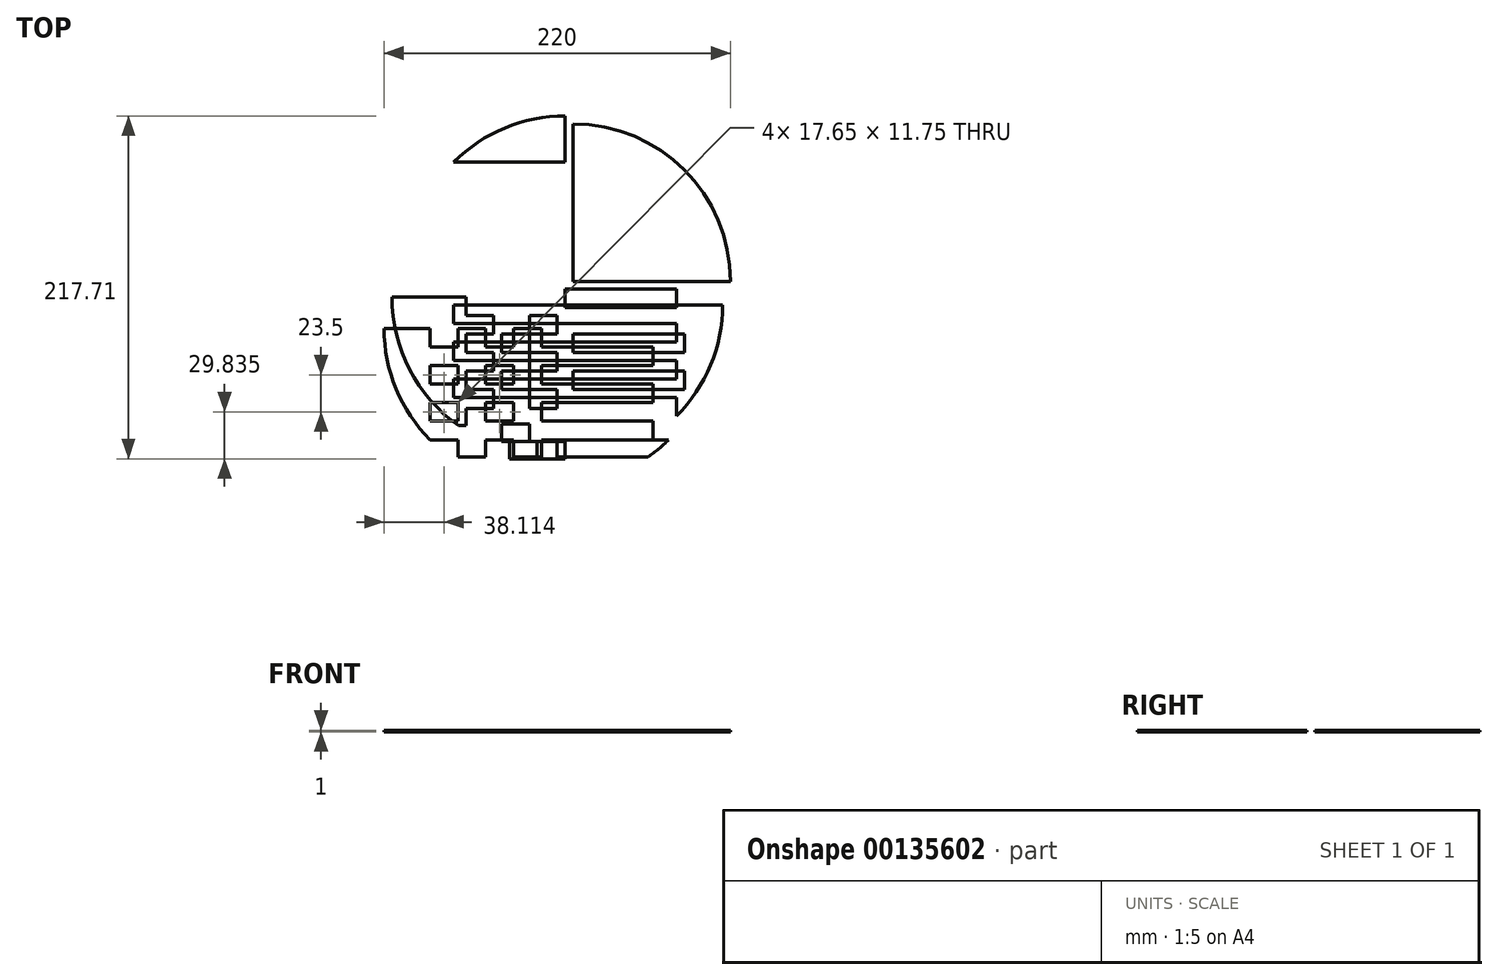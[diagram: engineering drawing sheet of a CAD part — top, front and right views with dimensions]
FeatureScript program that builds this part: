
annotation { "Feature Type Name" : "Feature", "Feature Type Description" : "" }
export const myFeature = defineFeature(function(context is Context, id is Id, definition is map)
    precondition{}
    {
        {
            var Q0;
            Q0=qCreatedBy(makeId("Top.planeOp"),FACE);
            var sketch = newSketch(context, id + "F0", { "sketchPlane" : qUnion([Q0])});
            skLineSegment(sketch, "E0.1", {"start": v(70.71, -70.71) * mm, "end": v(-70.71, -70.71) * mm});
            skLineSegment(sketch, "E0.2", {"start": v(-70.71, -70.71) * mm, "end": v(-70.71, 70.71) * mm});
            skLineSegment(sketch, "E1", {"start": v(70.71, 0) * mm, "end": v(-70.71, 0) * mm});
            skLineSegment(sketch, "E2", {"start": v(-14.1, -99) * mm, "end": v(14.1, -99) * mm});
            skLineSegment(sketch, "E3.0.1.0", {"start": v(70.71, -11.75) * mm, "end": v(-70.71, -11.75) * mm});
            skLineSegment(sketch, "E3.0.2.0", {"start": v(70.71, -23.5) * mm, "end": v(-70.71, -23.5) * mm});
            skLineSegment(sketch, "E3.0.3.0", {"start": v(70.71, -35.25) * mm, "end": v(-70.71, -35.25) * mm});
            skLineSegment(sketch, "E3.0.4.0", {"start": v(70.71, -47) * mm, "end": v(-70.71, -47) * mm});
            skLineSegment(sketch, "E3.0.5.0", {"start": v(70.71, -58.75) * mm, "end": v(-70.71, -58.75) * mm});
            skLineSegment(sketch, "E3.direction1", {"start": v(-70.71, 0) * mm, "end": v(-45.71, 0) * mm, "construction": true});
            skLineSegment(sketch, "E3.direction2", {"start": v(-70.71, 0) * mm, "end": v(-70.71, -11.75) * mm, "construction": true});
            skArc(sketch, "E4", {"start": v(-14.1, -99) * mm, "mid": v(0, 100) * mm, "end": v(14.1, -99) * mm});
            skLineSegment(sketch, "E5", {"start": v(0, 70.71) * mm, "end": v(0, -70.71) * mm});
            skLineSegment(sketch, "E6", {"start": v(57.65, -81.71) * mm, "end": v(-57.65, -81.71) * mm});
            skLineSegment(sketch, "E7", {"start": v(37.48, -92.71) * mm, "end": v(-37.48, -92.71) * mm});
            skLineSegment(sketch, "E8", {"start": v(0, -70.71) * mm, "end": v(0, -99) * mm});
            skLineSegment(sketch, "E9", {"start": v(-70.71, 0) * mm, "end": v(-100, 0) * mm});
            skLineSegment(sketch, "E10", {"start": v(70.71, 0) * mm, "end": v(100, 0) * mm});
            skLineSegment(sketch, "E11", {"start": v(0, 70.71) * mm, "end": v(0, 100) * mm});
            skLineSegment(sketch, "E12", {"start": v(-70.71, -70.71) * mm, "end": v(-70.71, 0) * mm});
            skLineSegment(sketch, "E13.1.0.0", {"start": v(-53.06, -70.71) * mm, "end": v(-53.06, 0) * mm});
            skLineSegment(sketch, "E13.2.0.0", {"start": v(-35.41, -70.71) * mm, "end": v(-35.41, 0) * mm});
            skLineSegment(sketch, "E13.3.0.0", {"start": v(-17.76, -70.71) * mm, "end": v(-17.76, 0) * mm});
            skLineSegment(sketch, "E13.direction1", {"start": v(-70.71, -70.71) * mm, "end": v(-53.06, -70.71) * mm, "construction": true});
            skLineSegment(sketch, "E14", {"start": v(-53.06, -70.71) * mm, "end": v(-53.06, -81.71) * mm});
            skLineSegment(sketch, "E15", {"start": v(-35.41, -70.71) * mm, "end": v(-35.41, -92.71) * mm});
            skLineSegment(sketch, "E16", {"start": v(-17.76, -70.71) * mm, "end": v(-17.76, -92.71) * mm});
            skLineSegment(sketch, "E17", {"start": v(0, 70.71) * mm, "end": v(-70.71, 70.71) * mm});
            skLineSegment(sketch, "E18", {"start": v(70.71, 0) * mm, "end": v(70.71, -70.71) * mm});
            skSolve(sketch);
        }
        {
            var Q0;
            {var subQ0=sQuery(id+"F0.wireOp",EDGE,"E10");Q0=makeQuery(id+"F0.imprint","IMPRINT",FACE,{"disambiguationData":[TD([[makeQuery(id+"F0.imprint","IMPRINT",EDGE,{"derivedFrom":subQ0}),1.0]])]});}
            var Q1;
            {var subQ0=sQuery(id+"F0.wireOp",EDGE,"E0.2");Q1=makeQuery(id+"F0.imprint","IMPRINT",FACE,{"disambiguationData":[TD([[makeQuery(id+"F0.imprint","IMPRINT",EDGE,{"derivedFrom":subQ0}),1.0]])]});}
            var Q2;
            {var subQ0=sQuery(id+"F0.wireOp",EDGE,"E18");var subQ1=sQuery(id+"F0.wireOp",EDGE,"E3.0.1.0");var subQ2=makeQuery(id+"F0.imprint","INTERSECT",VERTEX,{"derivedFrom":[subQ1,subQ0]});Q2=makeQuery(id+"F0.imprint","IMPRINT",FACE,{"disambiguationData":[TD([[makeQuery(id+"F0.imprint","IMPRINT",EDGE,{"disambiguationData":[TD([[subQ2,-1.0]])],"derivedFrom":subQ1}),1.0]])]});}
            var Q3;
            {var subQ0=sQuery(id+"F0.wireOp",EDGE,"E18");var subQ1=sQuery(id+"F0.wireOp",EDGE,"E3.0.3.0");var subQ2=makeQuery(id+"F0.imprint","INTERSECT",VERTEX,{"derivedFrom":[subQ1,subQ0]});Q3=makeQuery(id+"F0.imprint","IMPRINT",FACE,{"disambiguationData":[TD([[makeQuery(id+"F0.imprint","IMPRINT",EDGE,{"disambiguationData":[TD([[subQ2,-1.0]])],"derivedFrom":subQ1}),1.0]])]});}
            var Q4;
            {var subQ0=sQuery(id+"F0.wireOp",EDGE,"E18");var subQ5=sQuery(id+"F0.wireOp",EDGE,"E3.0.5.0");var subQ6=makeQuery(id+"F0.imprint","INTERSECT",VERTEX,{"derivedFrom":[subQ5,subQ0]});Q4=makeQuery(id+"F0.imprint","IMPRINT",FACE,{"disambiguationData":[TD([[makeQuery(id+"F0.imprint","IMPRINT",EDGE,{"disambiguationData":[TD([[subQ6,-1.0]])],"derivedFrom":subQ5}),1.0]])]});}
            var Q5;
            {var subQ0=sQuery(id+"F0.wireOp",EDGE,"E6");var subQ1=sQuery(id+"F0.wireOp",EDGE,"E4");var subQ2=makeQuery(id+"F0.imprint","INTERSECT",VERTEX,{"disambiguationData":[OD(0.0)],"derivedFrom":[subQ1,subQ0]});Q5=makeQuery(id+"F0.imprint","IMPRINT",FACE,{"disambiguationData":[TD([[makeQuery(id+"F0.imprint","IMPRINT",EDGE,{"disambiguationData":[TD([[subQ2,-1.0]])],"derivedFrom":subQ1}),-1.0]])]});}
            var Q6;
            {var subQ5=sQuery(id+"F0.wireOp",EDGE,"E4");var subQ6=sQuery(id+"F0.wireOp",EDGE,"E2");var subQ7=makeQuery(id+"F0.imprint","INTERSECT",VERTEX,{"disambiguationData":[OD(0.0)],"derivedFrom":[subQ6,subQ5]});Q6=makeQuery(id+"F0.imprint","IMPRINT",FACE,{"disambiguationData":[TD([[makeQuery(id+"F0.imprint","IMPRINT",EDGE,{"disambiguationData":[TD([[subQ7,-1.0]])],"derivedFrom":subQ6}),1.0]])]});}
            var Q7;
            {var subQ0=sQuery(id+"F0.wireOp",EDGE,"E8");var subQ5=sQuery(id+"F0.wireOp",EDGE,"E6");var subQ7=makeQuery(id+"F0.imprint","INTERSECT",VERTEX,{"derivedFrom":[subQ5,subQ0]});Q7=makeQuery(id+"F0.imprint","IMPRINT",FACE,{"disambiguationData":[TD([[makeQuery(id+"F0.imprint","IMPRINT",EDGE,{"disambiguationData":[TD([[subQ7,-1.0]])],"derivedFrom":subQ5}),-1.0]])]});}
            var Q8;
            {var subQ0=sQuery(id+"F0.wireOp",EDGE,"E5");var subQ1=sQuery(id+"F0.wireOp",EDGE,"E3.0.4.0");var subQ2=makeQuery(id+"F0.imprint","INTERSECT",VERTEX,{"derivedFrom":[subQ1,subQ0]});Q8=makeQuery(id+"F0.imprint","IMPRINT",FACE,{"disambiguationData":[TD([[makeQuery(id+"F0.imprint","IMPRINT",EDGE,{"disambiguationData":[TD([[subQ2,-1.0]])],"derivedFrom":subQ1}),1.0]])]});}
            var Q9;
            {var subQ0=sQuery(id+"F0.wireOp",EDGE,"E5");var subQ1=sQuery(id+"F0.wireOp",EDGE,"E3.0.2.0");var subQ2=makeQuery(id+"F0.imprint","INTERSECT",VERTEX,{"derivedFrom":[subQ1,subQ0]});Q9=makeQuery(id+"F0.imprint","IMPRINT",FACE,{"disambiguationData":[TD([[makeQuery(id+"F0.imprint","IMPRINT",EDGE,{"disambiguationData":[TD([[subQ2,-1.0]])],"derivedFrom":subQ1}),1.0]])]});}
            var Q10;
            {var subQ0=sQuery(id+"F0.wireOp",EDGE,"E13.3.0.0");var subQ1=sQuery(id+"F0.wireOp",EDGE,"E1");var subQ2=makeQuery(id+"F0.imprint","INTERSECT",VERTEX,{"derivedFrom":[subQ1,subQ0]});Q10=makeQuery(id+"F0.imprint","IMPRINT",FACE,{"disambiguationData":[TD([[makeQuery(id+"F0.imprint","IMPRINT",EDGE,{"disambiguationData":[TD([[subQ2,1.0]])],"derivedFrom":subQ1}),1.0]])]});}
            var Q11;
            {var subQ0=sQuery(id+"F0.wireOp",EDGE,"E13.3.0.0");var subQ1=sQuery(id+"F0.wireOp",EDGE,"E3.0.1.0");var subQ2=makeQuery(id+"F0.imprint","INTERSECT",VERTEX,{"derivedFrom":[subQ1,subQ0]});Q11=makeQuery(id+"F0.imprint","IMPRINT",FACE,{"disambiguationData":[TD([[makeQuery(id+"F0.imprint","IMPRINT",EDGE,{"disambiguationData":[TD([[subQ2,-1.0]])],"derivedFrom":subQ1}),1.0]])]});}
            var Q12;
            {var subQ0=sQuery(id+"F0.wireOp",EDGE,"E13.3.0.0");var subQ1=sQuery(id+"F0.wireOp",EDGE,"E3.0.3.0");var subQ2=makeQuery(id+"F0.imprint","INTERSECT",VERTEX,{"derivedFrom":[subQ1,subQ0]});Q12=makeQuery(id+"F0.imprint","IMPRINT",FACE,{"disambiguationData":[TD([[makeQuery(id+"F0.imprint","IMPRINT",EDGE,{"disambiguationData":[TD([[subQ2,-1.0]])],"derivedFrom":subQ1}),1.0]])]});}
            var Q13;
            {var subQ3=sQuery(id+"F0.wireOp",EDGE,"E13.3.0.0");var subQ5=sQuery(id+"F0.wireOp",EDGE,"E3.0.5.0");var subQ7=makeQuery(id+"F0.imprint","INTERSECT",VERTEX,{"derivedFrom":[subQ5,subQ3]});Q13=makeQuery(id+"F0.imprint","IMPRINT",FACE,{"disambiguationData":[TD([[makeQuery(id+"F0.imprint","IMPRINT",EDGE,{"disambiguationData":[TD([[subQ7,-1.0]])],"derivedFrom":subQ5}),1.0]])]});}
            var Q14;
            {var subQ0=sQuery(id+"F0.wireOp",EDGE,"E13.2.0.0");var subQ1=sQuery(id+"F0.wireOp",EDGE,"E3.0.4.0");var subQ2=makeQuery(id+"F0.imprint","INTERSECT",VERTEX,{"derivedFrom":[subQ1,subQ0]});Q14=makeQuery(id+"F0.imprint","IMPRINT",FACE,{"disambiguationData":[TD([[makeQuery(id+"F0.imprint","IMPRINT",EDGE,{"disambiguationData":[TD([[subQ2,-1.0]])],"derivedFrom":subQ1}),1.0]])]});}
            var Q15;
            {var subQ0=sQuery(id+"F0.wireOp",EDGE,"E13.2.0.0");var subQ1=sQuery(id+"F0.wireOp",EDGE,"E3.0.2.0");var subQ2=makeQuery(id+"F0.imprint","INTERSECT",VERTEX,{"derivedFrom":[subQ1,subQ0]});Q15=makeQuery(id+"F0.imprint","IMPRINT",FACE,{"disambiguationData":[TD([[makeQuery(id+"F0.imprint","IMPRINT",EDGE,{"disambiguationData":[TD([[subQ2,-1.0]])],"derivedFrom":subQ1}),1.0]])]});}
            var Q16;
            {var subQ0=sQuery(id+"F0.wireOp",EDGE,"E13.1.0.0");var subQ1=sQuery(id+"F0.wireOp",EDGE,"E1");var subQ2=makeQuery(id+"F0.imprint","INTERSECT",VERTEX,{"derivedFrom":[subQ1,subQ0]});Q16=makeQuery(id+"F0.imprint","IMPRINT",FACE,{"disambiguationData":[TD([[makeQuery(id+"F0.imprint","IMPRINT",EDGE,{"disambiguationData":[TD([[subQ2,1.0]])],"derivedFrom":subQ1}),1.0]])]});}
            var Q17;
            {var subQ0=sQuery(id+"F0.wireOp",EDGE,"E12");var subQ1=sQuery(id+"F0.wireOp",EDGE,"E3.0.1.0");var subQ2=makeQuery(id+"F0.imprint","INTERSECT",VERTEX,{"derivedFrom":[subQ1,subQ0]});Q17=makeQuery(id+"F0.imprint","IMPRINT",FACE,{"disambiguationData":[TD([[makeQuery(id+"F0.imprint","IMPRINT",EDGE,{"disambiguationData":[TD([[subQ2,1.0]])],"derivedFrom":subQ1}),1.0]])]});}
            var Q18;
            {var subQ0=sQuery(id+"F0.wireOp",EDGE,"E12");var subQ1=sQuery(id+"F0.wireOp",EDGE,"E3.0.3.0");var subQ2=makeQuery(id+"F0.imprint","INTERSECT",VERTEX,{"derivedFrom":[subQ1,subQ0]});Q18=makeQuery(id+"F0.imprint","IMPRINT",FACE,{"disambiguationData":[TD([[makeQuery(id+"F0.imprint","IMPRINT",EDGE,{"disambiguationData":[TD([[subQ2,1.0]])],"derivedFrom":subQ1}),1.0]])]});}
            var Q19;
            {var subQ0=sQuery(id+"F0.wireOp",EDGE,"E12");var subQ5=sQuery(id+"F0.wireOp",EDGE,"E3.0.5.0");var subQ6=makeQuery(id+"F0.imprint","INTERSECT",VERTEX,{"derivedFrom":[subQ5,subQ0]});Q19=makeQuery(id+"F0.imprint","IMPRINT",FACE,{"disambiguationData":[TD([[makeQuery(id+"F0.imprint","IMPRINT",EDGE,{"disambiguationData":[TD([[subQ6,1.0]])],"derivedFrom":subQ5}),1.0]])]});}
            var Q20;
            {var subQ0=sQuery(id+"F0.wireOp",EDGE,"E14");Q20=makeQuery(id+"F0.imprint","IMPRINT",FACE,{"disambiguationData":[TD([[makeQuery(id+"F0.imprint","IMPRINT",EDGE,{"derivedFrom":subQ0}),1.0]])]});}
            extrude(context, id + "F1", {"entities" : qUnion([Q0, Q1, Q2, Q3, Q4, Q5, Q6, Q7, Q8, Q9, Q10, Q11, Q12, Q13, Q14, Q15, Q16, Q17, Q18, Q19, Q20]), "depth" : 1 * mm});
        }
        {
            var Q0;
            {var subQ6=sQuery(id+"F0.wireOp",EDGE,"E0.2");Q0=makeQuery(id+"F0.imprint","IMPRINT",FACE,{"disambiguationData":[TD([[makeQuery(id+"F0.imprint","IMPRINT",EDGE,{"derivedFrom":subQ6}),-1.0]])]});}
            var Q1;
            {var subQ5=sQuery(id+"F0.wireOp",EDGE,"E9");Q1=makeQuery(id+"F0.imprint","IMPRINT",FACE,{"disambiguationData":[TD([[makeQuery(id+"F0.imprint","IMPRINT",EDGE,{"derivedFrom":subQ5}),1.0]])]});}
            var Q2;
            {var subQ0=sQuery(id+"F0.wireOp",EDGE,"E13.2.0.0");var subQ1=sQuery(id+"F0.wireOp",EDGE,"E3.0.1.0");var subQ2=makeQuery(id+"F0.imprint","INTERSECT",VERTEX,{"derivedFrom":[subQ1,subQ0]});Q2=makeQuery(id+"F0.imprint","IMPRINT",FACE,{"disambiguationData":[TD([[makeQuery(id+"F0.imprint","IMPRINT",EDGE,{"disambiguationData":[TD([[subQ2,-1.0]])],"derivedFrom":subQ1}),1.0]])]});}
            var Q3;
            {var subQ0=sQuery(id+"F0.wireOp",EDGE,"E13.2.0.0");var subQ1=sQuery(id+"F0.wireOp",EDGE,"E3.0.3.0");var subQ2=makeQuery(id+"F0.imprint","INTERSECT",VERTEX,{"derivedFrom":[subQ1,subQ0]});Q3=makeQuery(id+"F0.imprint","IMPRINT",FACE,{"disambiguationData":[TD([[makeQuery(id+"F0.imprint","IMPRINT",EDGE,{"disambiguationData":[TD([[subQ2,-1.0]])],"derivedFrom":subQ1}),1.0]])]});}
            var Q4;
            {var subQ3=sQuery(id+"F0.wireOp",EDGE,"E13.2.0.0");var subQ5=sQuery(id+"F0.wireOp",EDGE,"E3.0.5.0");var subQ6=makeQuery(id+"F0.imprint","INTERSECT",VERTEX,{"derivedFrom":[subQ5,subQ3]});Q4=makeQuery(id+"F0.imprint","IMPRINT",FACE,{"disambiguationData":[TD([[makeQuery(id+"F0.imprint","IMPRINT",EDGE,{"disambiguationData":[TD([[subQ6,-1.0]])],"derivedFrom":subQ5}),1.0]])]});}
            var Q5;
            {var subQ3=sQuery(id+"F0.wireOp",EDGE,"E14");Q5=makeQuery(id+"F0.imprint","IMPRINT",FACE,{"disambiguationData":[TD([[makeQuery(id+"F0.imprint","IMPRINT",EDGE,{"derivedFrom":subQ3}),-1.0]])]});}
            var Q6;
            {var subQ0=sQuery(id+"F0.wireOp",EDGE,"E16");var subQ1=sQuery(id+"F0.wireOp",EDGE,"E6");var subQ2=makeQuery(id+"F0.imprint","INTERSECT",VERTEX,{"derivedFrom":[subQ1,subQ0]});Q6=makeQuery(id+"F0.imprint","IMPRINT",FACE,{"disambiguationData":[TD([[makeQuery(id+"F0.imprint","IMPRINT",EDGE,{"disambiguationData":[TD([[subQ2,-1.0]])],"derivedFrom":subQ1}),1.0]])]});}
            var Q7;
            {var subQ0=sQuery(id+"F0.wireOp",EDGE,"E5");var subQ5=sQuery(id+"F0.wireOp",EDGE,"E3.0.5.0");var subQ6=makeQuery(id+"F0.imprint","INTERSECT",VERTEX,{"derivedFrom":[subQ5,subQ0]});Q7=makeQuery(id+"F0.imprint","IMPRINT",FACE,{"disambiguationData":[TD([[makeQuery(id+"F0.imprint","IMPRINT",EDGE,{"disambiguationData":[TD([[subQ6,-1.0]])],"derivedFrom":subQ5}),1.0]])]});}
            var Q8;
            {var subQ0=sQuery(id+"F0.wireOp",EDGE,"E13.3.0.0");var subQ1=sQuery(id+"F0.wireOp",EDGE,"E3.0.4.0");var subQ2=makeQuery(id+"F0.imprint","INTERSECT",VERTEX,{"derivedFrom":[subQ1,subQ0]});Q8=makeQuery(id+"F0.imprint","IMPRINT",FACE,{"disambiguationData":[TD([[makeQuery(id+"F0.imprint","IMPRINT",EDGE,{"disambiguationData":[TD([[subQ2,-1.0]])],"derivedFrom":subQ1}),1.0]])]});}
            var Q9;
            {var subQ0=sQuery(id+"F0.wireOp",EDGE,"E5");var subQ1=sQuery(id+"F0.wireOp",EDGE,"E3.0.3.0");var subQ2=makeQuery(id+"F0.imprint","INTERSECT",VERTEX,{"derivedFrom":[subQ1,subQ0]});Q9=makeQuery(id+"F0.imprint","IMPRINT",FACE,{"disambiguationData":[TD([[makeQuery(id+"F0.imprint","IMPRINT",EDGE,{"disambiguationData":[TD([[subQ2,-1.0]])],"derivedFrom":subQ1}),1.0]])]});}
            var Q10;
            {var subQ0=sQuery(id+"F0.wireOp",EDGE,"E13.3.0.0");var subQ1=sQuery(id+"F0.wireOp",EDGE,"E3.0.2.0");var subQ2=makeQuery(id+"F0.imprint","INTERSECT",VERTEX,{"derivedFrom":[subQ1,subQ0]});Q10=makeQuery(id+"F0.imprint","IMPRINT",FACE,{"disambiguationData":[TD([[makeQuery(id+"F0.imprint","IMPRINT",EDGE,{"disambiguationData":[TD([[subQ2,-1.0]])],"derivedFrom":subQ1}),1.0]])]});}
            var Q11;
            {var subQ0=sQuery(id+"F0.wireOp",EDGE,"E5");var subQ1=sQuery(id+"F0.wireOp",EDGE,"E3.0.1.0");var subQ2=makeQuery(id+"F0.imprint","INTERSECT",VERTEX,{"derivedFrom":[subQ1,subQ0]});Q11=makeQuery(id+"F0.imprint","IMPRINT",FACE,{"disambiguationData":[TD([[makeQuery(id+"F0.imprint","IMPRINT",EDGE,{"disambiguationData":[TD([[subQ2,-1.0]])],"derivedFrom":subQ1}),1.0]])]});}
            var Q12;
            {var subQ0=sQuery(id+"F0.wireOp",EDGE,"E18");var subQ5=sQuery(id+"F0.wireOp",EDGE,"E3.0.1.0");var subQ7=makeQuery(id+"F0.imprint","INTERSECT",VERTEX,{"derivedFrom":[subQ5,subQ0]});Q12=makeQuery(id+"F0.imprint","IMPRINT",FACE,{"disambiguationData":[TD([[makeQuery(id+"F0.imprint","IMPRINT",EDGE,{"disambiguationData":[TD([[subQ7,-1.0]])],"derivedFrom":subQ5}),-1.0]])]});}
            var Q13;
            {var subQ0=sQuery(id+"F0.wireOp",EDGE,"E18");var subQ1=sQuery(id+"F0.wireOp",EDGE,"E3.0.2.0");var subQ2=makeQuery(id+"F0.imprint","INTERSECT",VERTEX,{"derivedFrom":[subQ1,subQ0]});Q13=makeQuery(id+"F0.imprint","IMPRINT",FACE,{"disambiguationData":[TD([[makeQuery(id+"F0.imprint","IMPRINT",EDGE,{"disambiguationData":[TD([[subQ2,-1.0]])],"derivedFrom":subQ1}),1.0]])]});}
            var Q14;
            {var subQ0=sQuery(id+"F0.wireOp",EDGE,"E18");var subQ1=sQuery(id+"F0.wireOp",EDGE,"E3.0.4.0");var subQ2=makeQuery(id+"F0.imprint","INTERSECT",VERTEX,{"derivedFrom":[subQ1,subQ0]});Q14=makeQuery(id+"F0.imprint","IMPRINT",FACE,{"disambiguationData":[TD([[makeQuery(id+"F0.imprint","IMPRINT",EDGE,{"disambiguationData":[TD([[subQ2,-1.0]])],"derivedFrom":subQ1}),1.0]])]});}
            var Q15;
            {var subQ0=sQuery(id+"F0.wireOp",EDGE,"E4");var subQ5=sQuery(id+"F0.wireOp",EDGE,"E6");var subQ6=makeQuery(id+"F0.imprint","INTERSECT",VERTEX,{"disambiguationData":[OD(0.0)],"derivedFrom":[subQ0,subQ5]});Q15=makeQuery(id+"F0.imprint","IMPRINT",FACE,{"disambiguationData":[TD([[makeQuery(id+"F0.imprint","IMPRINT",EDGE,{"disambiguationData":[TD([[subQ6,-1.0]])],"derivedFrom":subQ5}),-1.0]])]});}
            var Q16;
            {var subQ0=sQuery(id+"F0.wireOp",EDGE,"E4");var subQ1=sQuery(id+"F0.wireOp",EDGE,"E2");var subQ2=makeQuery(id+"F0.imprint","INTERSECT",VERTEX,{"disambiguationData":[OD(1.0)],"derivedFrom":[subQ1,subQ0]});Q16=makeQuery(id+"F0.imprint","IMPRINT",FACE,{"disambiguationData":[TD([[makeQuery(id+"F0.imprint","IMPRINT",EDGE,{"disambiguationData":[TD([[subQ2,1.0]])],"derivedFrom":subQ1}),1.0]])]});}
            extrude(context, id + "F2", {"entities" : qUnion([Q0, Q1, Q2, Q3, Q4, Q5, Q6, Q7, Q8, Q9, Q10, Q11, Q12, Q13, Q14, Q15, Q16]), "depth" : 1 * mm});
        }
        {
            var Q0;
            {var subQ0=sQuery(id+"F0.wireOp",EDGE,"E12");var subQ5=sQuery(id+"F0.wireOp",EDGE,"E3.0.1.0");var subQ6=makeQuery(id+"F0.imprint","INTERSECT",VERTEX,{"derivedFrom":[subQ5,subQ0]});Q0=makeQuery(id+"F0.imprint","IMPRINT",FACE,{"disambiguationData":[TD([[makeQuery(id+"F0.imprint","IMPRINT",EDGE,{"disambiguationData":[TD([[subQ6,1.0]])],"derivedFrom":subQ5}),-1.0]])]});}
            var Q1;
            {var subQ0=sQuery(id+"F0.wireOp",EDGE,"E12");var subQ1=sQuery(id+"F0.wireOp",EDGE,"E3.0.2.0");var subQ2=makeQuery(id+"F0.imprint","INTERSECT",VERTEX,{"derivedFrom":[subQ1,subQ0]});Q1=makeQuery(id+"F0.imprint","IMPRINT",FACE,{"disambiguationData":[TD([[makeQuery(id+"F0.imprint","IMPRINT",EDGE,{"disambiguationData":[TD([[subQ2,1.0]])],"derivedFrom":subQ1}),1.0]])]});}
            var Q2;
            {var subQ0=sQuery(id+"F0.wireOp",EDGE,"E12");var subQ1=sQuery(id+"F0.wireOp",EDGE,"E3.0.4.0");var subQ2=makeQuery(id+"F0.imprint","INTERSECT",VERTEX,{"derivedFrom":[subQ1,subQ0]});Q2=makeQuery(id+"F0.imprint","IMPRINT",FACE,{"disambiguationData":[TD([[makeQuery(id+"F0.imprint","IMPRINT",EDGE,{"disambiguationData":[TD([[subQ2,1.0]])],"derivedFrom":subQ1}),1.0]])]});}
            var Q3;
            {var subQ0=sQuery(id+"F0.wireOp",EDGE,"E13.2.0.0");var subQ1=sQuery(id+"F0.wireOp",EDGE,"E1");var subQ2=makeQuery(id+"F0.imprint","INTERSECT",VERTEX,{"derivedFrom":[subQ1,subQ0]});Q3=makeQuery(id+"F0.imprint","IMPRINT",FACE,{"disambiguationData":[TD([[makeQuery(id+"F0.imprint","IMPRINT",EDGE,{"disambiguationData":[TD([[subQ2,1.0]])],"derivedFrom":subQ1}),1.0]])]});}
            var Q4;
            {var subQ3=sQuery(id+"F0.wireOp",EDGE,"E16");var subQ5=sQuery(id+"F0.wireOp",EDGE,"E6");var subQ6=makeQuery(id+"F0.imprint","INTERSECT",VERTEX,{"derivedFrom":[subQ5,subQ3]});Q4=makeQuery(id+"F0.imprint","IMPRINT",FACE,{"disambiguationData":[TD([[makeQuery(id+"F0.imprint","IMPRINT",EDGE,{"disambiguationData":[TD([[subQ6,-1.0]])],"derivedFrom":subQ5}),-1.0]])]});}
            var Q5;
            {var subQ1=sQuery(id+"F0.wireOp",EDGE,"E4");var subQ5=sQuery(id+"F0.wireOp",EDGE,"E6");var subQ6=makeQuery(id+"F0.imprint","INTERSECT",VERTEX,{"disambiguationData":[OD(1.0)],"derivedFrom":[subQ1,subQ5]});Q5=makeQuery(id+"F0.imprint","IMPRINT",FACE,{"disambiguationData":[TD([[makeQuery(id+"F0.imprint","IMPRINT",EDGE,{"disambiguationData":[TD([[subQ6,1.0]])],"derivedFrom":subQ1}),-1.0]])]});}
            var Q6;
            {var subQ0=sQuery(id+"F0.wireOp",EDGE,"E8");var subQ1=sQuery(id+"F0.wireOp",EDGE,"E6");var subQ2=makeQuery(id+"F0.imprint","INTERSECT",VERTEX,{"derivedFrom":[subQ1,subQ0]});Q6=makeQuery(id+"F0.imprint","IMPRINT",FACE,{"disambiguationData":[TD([[makeQuery(id+"F0.imprint","IMPRINT",EDGE,{"disambiguationData":[TD([[subQ2,-1.0]])],"derivedFrom":subQ1}),1.0]])]});}
            var Q7;
            {var subQ6=sQuery(id+"F0.wireOp",EDGE,"E10");Q7=makeQuery(id+"F0.imprint","IMPRINT",FACE,{"disambiguationData":[TD([[makeQuery(id+"F0.imprint","IMPRINT",EDGE,{"derivedFrom":subQ6}),-1.0]])]});}
            extrude(context, id + "F3", {"entities" : qUnion([Q0, Q1, Q2, Q3, Q4, Q5, Q6, Q7]), "depth" : 1 * mm});
        }
        {
            var Q0;
            {var subQ2=sQuery(id+"F0.wireOp",EDGE,"E11");Q0=makeQuery(id+"F0.imprint","IMPRINT",FACE,{"disambiguationData":[TD([[makeQuery(id+"F0.imprint","IMPRINT",EDGE,{"derivedFrom":subQ2}),1.0]])]});}
            extrude(context, id + "F4", {"entities" : qUnion([Q0]), "depth" : 1 * mm});
        }
        {
            assignVariable(context, id + "F5", {"name" : "d", "anyValue" : 5 * mm});
        }
        {
            var Q0;
            Q0=makeQuery(id+"F2.opExtrude","SWEPT_BODY",BODY,{"disambiguationData":[OSD([sQuery(id+"F0.wireOp",EDGE,"E0.2"),sQuery(id+"F0.wireOp",EDGE,"E1"),sQuery(id+"F0.wireOp",EDGE,"E5"),sQuery(id+"F0.wireOp",EDGE,"E17")])]});
            var Q1;
            Q1=makeQuery(id+"F1.opExtrude","SWEPT_BODY",BODY,{"disambiguationData":[OSD([sQuery(id+"F0.wireOp",EDGE,"E0.2"),sQuery(id+"F0.wireOp",EDGE,"E4"),sQuery(id+"F0.wireOp",EDGE,"E9")])]});
            var Q2;
            Q2=makeQuery(id+"F4.opExtrude","SWEPT_BODY",BODY,{"disambiguationData":[OSD([sQuery(id+"F0.wireOp",EDGE,"E4"),sQuery(id+"F0.wireOp",EDGE,"E11"),sQuery(id+"F0.wireOp",EDGE,"E17")])]});
            var Q3;
            Q3=sQuery(id+"F0.wireOp",EDGE,"E5");
            transform(context, id + "F6", {"entities" : qUnion([Q0, Q1, Q2]), "transformType" : TransformType.TRANSLATION_3D, "dx" : -getVariable(context, 'd'), "dy" : 0 * mm, "dz" : 0 * mm, "makeCopy" : false});
        }
        {
            var Q0;
            Q0=makeQuery(id+"F3.opExtrude","SWEPT_BODY",BODY,{"disambiguationData":[OSD([sQuery(id+"F0.wireOp",EDGE,"E0.1"),sQuery(id+"F0.wireOp",EDGE,"E6"),sQuery(id+"F0.wireOp",EDGE,"E15"),sQuery(id+"F0.wireOp",EDGE,"E16")])]});
            var Q1;
            Q1=makeQuery(id+"F1.opExtrude","SWEPT_BODY",BODY,{"disambiguationData":[OSD([sQuery(id+"F0.wireOp",EDGE,"E0.1"),sQuery(id+"F0.wireOp",EDGE,"E3.0.5.0"),sQuery(id+"F0.wireOp",EDGE,"E13.2.0.0"),sQuery(id+"F0.wireOp",EDGE,"E13.3.0.0")])]});
            var Q2;
            Q2=makeQuery(id+"F1.opExtrude","SWEPT_BODY",BODY,{"disambiguationData":[OSD([sQuery(id+"F0.wireOp",EDGE,"E0.1"),sQuery(id+"F0.wireOp",EDGE,"E6"),sQuery(id+"F0.wireOp",EDGE,"E8"),sQuery(id+"F0.wireOp",EDGE,"E16")])]});
            var Q3;
            Q3=makeQuery(id+"F1.opExtrude","SWEPT_BODY",BODY,{"disambiguationData":[OSD([sQuery(id+"F0.wireOp",EDGE,"E0.1"),sQuery(id+"F0.wireOp",EDGE,"E6"),sQuery(id+"F0.wireOp",EDGE,"E14"),sQuery(id+"F0.wireOp",EDGE,"E15")])]});
            var Q4;
            Q4=makeQuery(id+"F1.opExtrude","SWEPT_BODY",BODY,{"disambiguationData":[OSD([sQuery(id+"F0.wireOp",EDGE,"E0.1"),sQuery(id+"F0.wireOp",EDGE,"E3.0.5.0"),sQuery(id+"F0.wireOp",EDGE,"E12"),sQuery(id+"F0.wireOp",EDGE,"E13.1.0.0")])]});
            var Q5;
            Q5=makeQuery(id+"F1.opExtrude","SWEPT_BODY",BODY,{"disambiguationData":[OSD([sQuery(id+"F0.wireOp",EDGE,"E1"),sQuery(id+"F0.wireOp",EDGE,"E3.0.1.0"),sQuery(id+"F0.wireOp",EDGE,"E5"),sQuery(id+"F0.wireOp",EDGE,"E13.3.0.0")])]});
            var Q6;
            Q6=makeQuery(id+"F1.opExtrude","SWEPT_BODY",BODY,{"disambiguationData":[OSD([sQuery(id+"F0.wireOp",EDGE,"E1"),sQuery(id+"F0.wireOp",EDGE,"E3.0.1.0"),sQuery(id+"F0.wireOp",EDGE,"E13.1.0.0"),sQuery(id+"F0.wireOp",EDGE,"E13.2.0.0")])]});
            var Q7;
            Q7=makeQuery(id+"F1.opExtrude","SWEPT_BODY",BODY,{"disambiguationData":[OSD([sQuery(id+"F0.wireOp",EDGE,"E2"),sQuery(id+"F0.wireOp",EDGE,"E4"),sQuery(id+"F0.wireOp",EDGE,"E7"),sQuery(id+"F0.wireOp",EDGE,"E8")])]});
            var Q8;
            Q8=makeQuery(id+"F1.opExtrude","SWEPT_BODY",BODY,{"disambiguationData":[OSD([sQuery(id+"F0.wireOp",EDGE,"E3.0.1.0"),sQuery(id+"F0.wireOp",EDGE,"E3.0.2.0"),sQuery(id+"F0.wireOp",EDGE,"E13.2.0.0"),sQuery(id+"F0.wireOp",EDGE,"E13.3.0.0")])]});
            var Q9;
            Q9=makeQuery(id+"F1.opExtrude","SWEPT_BODY",BODY,{"disambiguationData":[OSD([sQuery(id+"F0.wireOp",EDGE,"E3.0.1.0"),sQuery(id+"F0.wireOp",EDGE,"E3.0.2.0"),sQuery(id+"F0.wireOp",EDGE,"E12"),sQuery(id+"F0.wireOp",EDGE,"E13.1.0.0")])]});
            var Q10;
            Q10=makeQuery(id+"F1.opExtrude","SWEPT_BODY",BODY,{"disambiguationData":[OSD([sQuery(id+"F0.wireOp",EDGE,"E3.0.2.0"),sQuery(id+"F0.wireOp",EDGE,"E3.0.3.0"),sQuery(id+"F0.wireOp",EDGE,"E5"),sQuery(id+"F0.wireOp",EDGE,"E13.3.0.0")])]});
            var Q11;
            Q11=makeQuery(id+"F1.opExtrude","SWEPT_BODY",BODY,{"disambiguationData":[OSD([sQuery(id+"F0.wireOp",EDGE,"E3.0.2.0"),sQuery(id+"F0.wireOp",EDGE,"E3.0.3.0"),sQuery(id+"F0.wireOp",EDGE,"E13.1.0.0"),sQuery(id+"F0.wireOp",EDGE,"E13.2.0.0")])]});
            var Q12;
            Q12=makeQuery(id+"F1.opExtrude","SWEPT_BODY",BODY,{"disambiguationData":[OSD([sQuery(id+"F0.wireOp",EDGE,"E3.0.3.0"),sQuery(id+"F0.wireOp",EDGE,"E3.0.4.0"),sQuery(id+"F0.wireOp",EDGE,"E13.2.0.0"),sQuery(id+"F0.wireOp",EDGE,"E13.3.0.0")])]});
            var Q13;
            Q13=makeQuery(id+"F1.opExtrude","SWEPT_BODY",BODY,{"disambiguationData":[OSD([sQuery(id+"F0.wireOp",EDGE,"E3.0.3.0"),sQuery(id+"F0.wireOp",EDGE,"E3.0.4.0"),sQuery(id+"F0.wireOp",EDGE,"E12"),sQuery(id+"F0.wireOp",EDGE,"E13.1.0.0")])]});
            var Q14;
            Q14=makeQuery(id+"F1.opExtrude","SWEPT_BODY",BODY,{"disambiguationData":[OSD([sQuery(id+"F0.wireOp",EDGE,"E3.0.4.0"),sQuery(id+"F0.wireOp",EDGE,"E3.0.5.0"),sQuery(id+"F0.wireOp",EDGE,"E5"),sQuery(id+"F0.wireOp",EDGE,"E13.3.0.0")])]});
            var Q15;
            Q15=makeQuery(id+"F2.opExtrude","SWEPT_BODY",BODY,{"disambiguationData":[OSD([sQuery(id+"F0.wireOp",EDGE,"E0.1"),sQuery(id+"F0.wireOp",EDGE,"E3.0.5.0"),sQuery(id+"F0.wireOp",EDGE,"E13.1.0.0"),sQuery(id+"F0.wireOp",EDGE,"E13.2.0.0")])]});
            var Q16;
            Q16=makeQuery(id+"F2.opExtrude","SWEPT_BODY",BODY,{"disambiguationData":[OSD([sQuery(id+"F0.wireOp",EDGE,"E0.1"),sQuery(id+"F0.wireOp",EDGE,"E3.0.5.0"),sQuery(id+"F0.wireOp",EDGE,"E5"),sQuery(id+"F0.wireOp",EDGE,"E13.3.0.0")])]});
            var Q17;
            Q17=makeQuery(id+"F2.opExtrude","SWEPT_BODY",BODY,{"disambiguationData":[OSD([sQuery(id+"F0.wireOp",EDGE,"E0.1"),sQuery(id+"F0.wireOp",EDGE,"E4"),sQuery(id+"F0.wireOp",EDGE,"E6"),sQuery(id+"F0.wireOp",EDGE,"E14")])]});
            var Q18;
            Q18=makeQuery(id+"F3.opExtrude","SWEPT_BODY",BODY,{"disambiguationData":[OSD([sQuery(id+"F0.wireOp",EDGE,"E1"),sQuery(id+"F0.wireOp",EDGE,"E3.0.1.0"),sQuery(id+"F0.wireOp",EDGE,"E12"),sQuery(id+"F0.wireOp",EDGE,"E13.1.0.0")])]});
            var Q19;
            Q19=makeQuery(id+"F3.opExtrude","SWEPT_BODY",BODY,{"disambiguationData":[OSD([sQuery(id+"F0.wireOp",EDGE,"E1"),sQuery(id+"F0.wireOp",EDGE,"E3.0.1.0"),sQuery(id+"F0.wireOp",EDGE,"E13.2.0.0"),sQuery(id+"F0.wireOp",EDGE,"E13.3.0.0")])]});
            var Q20;
            Q20=makeQuery(id+"F3.opExtrude","SWEPT_BODY",BODY,{"disambiguationData":[OSD([sQuery(id+"F0.wireOp",EDGE,"E3.0.2.0"),sQuery(id+"F0.wireOp",EDGE,"E3.0.3.0"),sQuery(id+"F0.wireOp",EDGE,"E12"),sQuery(id+"F0.wireOp",EDGE,"E13.1.0.0")])]});
            var Q21;
            Q21=makeQuery(id+"F3.opExtrude","SWEPT_BODY",BODY,{"disambiguationData":[OSD([sQuery(id+"F0.wireOp",EDGE,"E3.0.4.0"),sQuery(id+"F0.wireOp",EDGE,"E3.0.5.0"),sQuery(id+"F0.wireOp",EDGE,"E12"),sQuery(id+"F0.wireOp",EDGE,"E13.1.0.0")])]});
            var Q22;
            Q22=makeQuery(id+"F3.opExtrude","SWEPT_BODY",BODY,{"disambiguationData":[OSD([sQuery(id+"F0.wireOp",EDGE,"E4"),sQuery(id+"F0.wireOp",EDGE,"E6"),sQuery(id+"F0.wireOp",EDGE,"E7"),sQuery(id+"F0.wireOp",EDGE,"E15")])]});
            var Q23;
            Q23=makeQuery(id+"F3.opExtrude","SWEPT_BODY",BODY,{"disambiguationData":[OSD([sQuery(id+"F0.wireOp",EDGE,"E6"),sQuery(id+"F0.wireOp",EDGE,"E7"),sQuery(id+"F0.wireOp",EDGE,"E8"),sQuery(id+"F0.wireOp",EDGE,"E16")])]});
            var Q24;
            Q24=makeQuery(id+"F2.opExtrude","SWEPT_BODY",BODY,{"disambiguationData":[OSD([sQuery(id+"F0.wireOp",EDGE,"E3.0.1.0"),sQuery(id+"F0.wireOp",EDGE,"E3.0.2.0"),sQuery(id+"F0.wireOp",EDGE,"E13.1.0.0"),sQuery(id+"F0.wireOp",EDGE,"E13.2.0.0")])]});
            var Q25;
            Q25=makeQuery(id+"F2.opExtrude","SWEPT_BODY",BODY,{"disambiguationData":[OSD([sQuery(id+"F0.wireOp",EDGE,"E6"),sQuery(id+"F0.wireOp",EDGE,"E7"),sQuery(id+"F0.wireOp",EDGE,"E15"),sQuery(id+"F0.wireOp",EDGE,"E16")])]});
            var Q26;
            Q26=makeQuery(id+"F2.opExtrude","SWEPT_BODY",BODY,{"disambiguationData":[OSD([sQuery(id+"F0.wireOp",EDGE,"E4"),sQuery(id+"F0.wireOp",EDGE,"E9"),sQuery(id+"F0.wireOp",EDGE,"E12")])]});
            var Q27;
            Q27=makeQuery(id+"F2.opExtrude","SWEPT_BODY",BODY,{"disambiguationData":[OSD([sQuery(id+"F0.wireOp",EDGE,"E3.0.1.0"),sQuery(id+"F0.wireOp",EDGE,"E3.0.2.0"),sQuery(id+"F0.wireOp",EDGE,"E5"),sQuery(id+"F0.wireOp",EDGE,"E13.3.0.0")])]});
            var Q28;
            Q28=makeQuery(id+"F2.opExtrude","SWEPT_BODY",BODY,{"disambiguationData":[OSD([sQuery(id+"F0.wireOp",EDGE,"E3.0.4.0"),sQuery(id+"F0.wireOp",EDGE,"E3.0.5.0"),sQuery(id+"F0.wireOp",EDGE,"E13.2.0.0"),sQuery(id+"F0.wireOp",EDGE,"E13.3.0.0")])]});
            var Q29;
            Q29=makeQuery(id+"F2.opExtrude","SWEPT_BODY",BODY,{"disambiguationData":[OSD([sQuery(id+"F0.wireOp",EDGE,"E3.0.3.0"),sQuery(id+"F0.wireOp",EDGE,"E3.0.4.0"),sQuery(id+"F0.wireOp",EDGE,"E13.1.0.0"),sQuery(id+"F0.wireOp",EDGE,"E13.2.0.0")])]});
            var Q30;
            Q30=makeQuery(id+"F2.opExtrude","SWEPT_BODY",BODY,{"disambiguationData":[OSD([sQuery(id+"F0.wireOp",EDGE,"E3.0.3.0"),sQuery(id+"F0.wireOp",EDGE,"E3.0.4.0"),sQuery(id+"F0.wireOp",EDGE,"E5"),sQuery(id+"F0.wireOp",EDGE,"E13.3.0.0")])]});
            var Q31;
            Q31=makeQuery(id+"F2.opExtrude","SWEPT_BODY",BODY,{"disambiguationData":[OSD([sQuery(id+"F0.wireOp",EDGE,"E3.0.2.0"),sQuery(id+"F0.wireOp",EDGE,"E3.0.3.0"),sQuery(id+"F0.wireOp",EDGE,"E13.2.0.0"),sQuery(id+"F0.wireOp",EDGE,"E13.3.0.0")])]});
            var Q32;
            Q32=makeQuery(id+"F1.opExtrude","SWEPT_BODY",BODY,{"disambiguationData":[OSD([sQuery(id+"F0.wireOp",EDGE,"E3.0.4.0"),sQuery(id+"F0.wireOp",EDGE,"E3.0.5.0"),sQuery(id+"F0.wireOp",EDGE,"E13.1.0.0"),sQuery(id+"F0.wireOp",EDGE,"E13.2.0.0")])]});
            transform(context, id + "F7", {"entities" : qUnion([Q0, Q1, Q2, Q3, Q4, Q5, Q6, Q7, Q8, Q9, Q10, Q11, Q12, Q13, Q14, Q15, Q16, Q17, Q18, Q19, Q20, Q21, Q22, Q23, Q24, Q25, Q26, Q27, Q28, Q29, Q30, Q31, Q32]), "transformType" : TransformType.TRANSLATION_3D, "dx" : -getVariable(context, 'd'), "dy" : -getVariable(context, 'd'), "dz" : 0 * mm, "makeCopy" : false});
        }
        {
            var Q0;
            Q0=makeQuery(id+"F1.opExtrude","SWEPT_BODY",BODY,{"disambiguationData":[OSD([sQuery(id+"F0.wireOp",EDGE,"E0.1"),sQuery(id+"F0.wireOp",EDGE,"E3.0.5.0"),sQuery(id+"F0.wireOp",EDGE,"E5"),sQuery(id+"F0.wireOp",EDGE,"E18")])]});
            var Q1;
            Q1=makeQuery(id+"F2.opExtrude","SWEPT_BODY",BODY,{"disambiguationData":[OSD([sQuery(id+"F0.wireOp",EDGE,"E0.1"),sQuery(id+"F0.wireOp",EDGE,"E4"),sQuery(id+"F0.wireOp",EDGE,"E6"),sQuery(id+"F0.wireOp",EDGE,"E8")])]});
            var Q2;
            Q2=makeQuery(id+"F1.opExtrude","SWEPT_BODY",BODY,{"disambiguationData":[OSD([sQuery(id+"F0.wireOp",EDGE,"E4"),sQuery(id+"F0.wireOp",EDGE,"E6"),sQuery(id+"F0.wireOp",EDGE,"E7"),sQuery(id+"F0.wireOp",EDGE,"E8")])]});
            var Q3;
            Q3=makeQuery(id+"F1.opExtrude","SWEPT_BODY",BODY,{"disambiguationData":[OSD([sQuery(id+"F0.wireOp",EDGE,"E3.0.1.0"),sQuery(id+"F0.wireOp",EDGE,"E3.0.2.0"),sQuery(id+"F0.wireOp",EDGE,"E5"),sQuery(id+"F0.wireOp",EDGE,"E18")])]});
            var Q4;
            Q4=makeQuery(id+"F1.opExtrude","SWEPT_BODY",BODY,{"disambiguationData":[OSD([sQuery(id+"F0.wireOp",EDGE,"E3.0.3.0"),sQuery(id+"F0.wireOp",EDGE,"E3.0.4.0"),sQuery(id+"F0.wireOp",EDGE,"E5"),sQuery(id+"F0.wireOp",EDGE,"E18")])]});
            var Q5;
            Q5=makeQuery(id+"F2.opExtrude","SWEPT_BODY",BODY,{"disambiguationData":[OSD([sQuery(id+"F0.wireOp",EDGE,"E1"),sQuery(id+"F0.wireOp",EDGE,"E3.0.1.0"),sQuery(id+"F0.wireOp",EDGE,"E5"),sQuery(id+"F0.wireOp",EDGE,"E18")])]});
            var Q6;
            Q6=makeQuery(id+"F3.opExtrude","SWEPT_BODY",BODY,{"disambiguationData":[OSD([sQuery(id+"F0.wireOp",EDGE,"E4"),sQuery(id+"F0.wireOp",EDGE,"E10"),sQuery(id+"F0.wireOp",EDGE,"E18")])]});
            var Q7;
            Q7=makeQuery(id+"F2.opExtrude","SWEPT_BODY",BODY,{"disambiguationData":[OSD([sQuery(id+"F0.wireOp",EDGE,"E2"),sQuery(id+"F0.wireOp",EDGE,"E4"),sQuery(id+"F0.wireOp",EDGE,"E7"),sQuery(id+"F0.wireOp",EDGE,"E8")])]});
            var Q8;
            Q8=makeQuery(id+"F2.opExtrude","SWEPT_BODY",BODY,{"disambiguationData":[OSD([sQuery(id+"F0.wireOp",EDGE,"E3.0.4.0"),sQuery(id+"F0.wireOp",EDGE,"E3.0.5.0"),sQuery(id+"F0.wireOp",EDGE,"E5"),sQuery(id+"F0.wireOp",EDGE,"E18")])]});
            var Q9;
            Q9=makeQuery(id+"F2.opExtrude","SWEPT_BODY",BODY,{"disambiguationData":[OSD([sQuery(id+"F0.wireOp",EDGE,"E3.0.2.0"),sQuery(id+"F0.wireOp",EDGE,"E3.0.3.0"),sQuery(id+"F0.wireOp",EDGE,"E5"),sQuery(id+"F0.wireOp",EDGE,"E18")])]});
            transform(context, id + "F8", {"entities" : qUnion([Q0, Q1, Q2, Q3, Q4, Q5, Q6, Q7, Q8, Q9]), "transformType" : TransformType.TRANSLATION_3D, "dx" : 0 * mm, "dy" : -getVariable(context, 'd'), "dz" : 0 * mm, "makeCopy" : false});
        }
        {
            var Q0;
            Q0=makeQuery(id+"F4.opExtrude","SWEPT_BODY",BODY,{"disambiguationData":[OSD([sQuery(id+"F0.wireOp",EDGE,"E4"),sQuery(id+"F0.wireOp",EDGE,"E11"),sQuery(id+"F0.wireOp",EDGE,"E17")])]});
            transform(context, id + "F9", {"entities" : qUnion([Q0]), "transformType" : TransformType.TRANSLATION_3D, "dx" : 0 * mm, "dy" : getVariable(context, 'd'), "dz" : 0 * mm, "makeCopy" : false});
        }
        {
            var Q0;
            Q0=makeQuery(id+"F1.opExtrude","SWEPT_BODY",BODY,{"disambiguationData":[OSD([sQuery(id+"F0.wireOp",EDGE,"E0.2"),sQuery(id+"F0.wireOp",EDGE,"E4"),sQuery(id+"F0.wireOp",EDGE,"E9")])]});
            transform(context, id + "F10", {"entities" : qUnion([Q0]), "transformType" : TransformType.TRANSLATION_3D, "dx" : -getVariable(context, 'd'), "dy" : 0 * mm, "dz" : 0 * mm, "makeCopy" : false});
        }
        {
            var Q0;
            Q0=makeQuery(id+"F3.opExtrude","SWEPT_BODY",BODY,{"disambiguationData":[OSD([sQuery(id+"F0.wireOp",EDGE,"E4"),sQuery(id+"F0.wireOp",EDGE,"E10"),sQuery(id+"F0.wireOp",EDGE,"E18")])]});
            transform(context, id + "F11", {"entities" : qUnion([Q0]), "transformType" : TransformType.TRANSLATION_3D, "dx" : getVariable(context, 'd'), "dy" : 0 * mm, "dz" : 0 * mm, "makeCopy" : false});
        }
        {
            var Q0;
            Q0=makeQuery(id+"F2.opExtrude","SWEPT_BODY",BODY,{"disambiguationData":[OSD([sQuery(id+"F0.wireOp",EDGE,"E0.1"),sQuery(id+"F0.wireOp",EDGE,"E4"),sQuery(id+"F0.wireOp",EDGE,"E6"),sQuery(id+"F0.wireOp",EDGE,"E8")])]});
            var Q1;
            Q1=makeQuery(id+"F1.opExtrude","SWEPT_BODY",BODY,{"disambiguationData":[OSD([sQuery(id+"F0.wireOp",EDGE,"E4"),sQuery(id+"F0.wireOp",EDGE,"E6"),sQuery(id+"F0.wireOp",EDGE,"E7"),sQuery(id+"F0.wireOp",EDGE,"E8")])]});
            var Q2;
            Q2=makeQuery(id+"F2.opExtrude","SWEPT_BODY",BODY,{"disambiguationData":[OSD([sQuery(id+"F0.wireOp",EDGE,"E2"),sQuery(id+"F0.wireOp",EDGE,"E4"),sQuery(id+"F0.wireOp",EDGE,"E7"),sQuery(id+"F0.wireOp",EDGE,"E8")])]});
            transform(context, id + "F12", {"entities" : qUnion([Q0, Q1, Q2]), "transformType" : TransformType.TRANSLATION_3D, "dx" : 0 * mm, "dy" : -getVariable(context, 'd'), "dz" : 0 * mm, "makeCopy" : false});
        }
        {
            var Q0;
            Q0=makeQuery(id+"F2.opExtrude","SWEPT_BODY",BODY,{"disambiguationData":[OSD([sQuery(id+"F0.wireOp",EDGE,"E4"),sQuery(id+"F0.wireOp",EDGE,"E9"),sQuery(id+"F0.wireOp",EDGE,"E12")])]});
            transform(context, id + "F13", {"entities" : qUnion([Q0]), "transformType" : TransformType.TRANSLATION_3D, "dx" : -getVariable(context, 'd'), "dy" : 0 * mm, "dz" : 0 * mm, "makeCopy" : false});
        }
        {
            var Q0;
            Q0=makeQuery(id+"F3.opExtrude","SWEPT_BODY",BODY,{"disambiguationData":[OSD([sQuery(id+"F0.wireOp",EDGE,"E0.1"),sQuery(id+"F0.wireOp",EDGE,"E6"),sQuery(id+"F0.wireOp",EDGE,"E15"),sQuery(id+"F0.wireOp",EDGE,"E16")])]});
            var Q1;
            Q1=makeQuery(id+"F1.opExtrude","SWEPT_BODY",BODY,{"disambiguationData":[OSD([sQuery(id+"F0.wireOp",EDGE,"E0.1"),sQuery(id+"F0.wireOp",EDGE,"E6"),sQuery(id+"F0.wireOp",EDGE,"E8"),sQuery(id+"F0.wireOp",EDGE,"E16")])]});
            var Q2;
            Q2=makeQuery(id+"F1.opExtrude","SWEPT_BODY",BODY,{"disambiguationData":[OSD([sQuery(id+"F0.wireOp",EDGE,"E0.1"),sQuery(id+"F0.wireOp",EDGE,"E6"),sQuery(id+"F0.wireOp",EDGE,"E14"),sQuery(id+"F0.wireOp",EDGE,"E15")])]});
            var Q3;
            Q3=makeQuery(id+"F1.opExtrude","SWEPT_BODY",BODY,{"disambiguationData":[OSD([sQuery(id+"F0.wireOp",EDGE,"E2"),sQuery(id+"F0.wireOp",EDGE,"E4"),sQuery(id+"F0.wireOp",EDGE,"E7"),sQuery(id+"F0.wireOp",EDGE,"E8")])]});
            var Q4;
            Q4=makeQuery(id+"F2.opExtrude","SWEPT_BODY",BODY,{"disambiguationData":[OSD([sQuery(id+"F0.wireOp",EDGE,"E0.1"),sQuery(id+"F0.wireOp",EDGE,"E4"),sQuery(id+"F0.wireOp",EDGE,"E6"),sQuery(id+"F0.wireOp",EDGE,"E14")])]});
            var Q5;
            Q5=makeQuery(id+"F3.opExtrude","SWEPT_BODY",BODY,{"disambiguationData":[OSD([sQuery(id+"F0.wireOp",EDGE,"E4"),sQuery(id+"F0.wireOp",EDGE,"E6"),sQuery(id+"F0.wireOp",EDGE,"E7"),sQuery(id+"F0.wireOp",EDGE,"E15")])]});
            var Q6;
            Q6=makeQuery(id+"F3.opExtrude","SWEPT_BODY",BODY,{"disambiguationData":[OSD([sQuery(id+"F0.wireOp",EDGE,"E6"),sQuery(id+"F0.wireOp",EDGE,"E7"),sQuery(id+"F0.wireOp",EDGE,"E8"),sQuery(id+"F0.wireOp",EDGE,"E16")])]});
            var Q7;
            Q7=makeQuery(id+"F2.opExtrude","SWEPT_BODY",BODY,{"disambiguationData":[OSD([sQuery(id+"F0.wireOp",EDGE,"E6"),sQuery(id+"F0.wireOp",EDGE,"E7"),sQuery(id+"F0.wireOp",EDGE,"E15"),sQuery(id+"F0.wireOp",EDGE,"E16")])]});
            transform(context, id + "F14", {"entities" : qUnion([Q0, Q1, Q2, Q3, Q4, Q5, Q6, Q7]), "transformType" : TransformType.TRANSLATION_3D, "dx" : 0 * mm, "dy" : -getVariable(context, 'd'), "dz" : 0 * mm, "makeCopy" : false});
        }
        {
            var Q0;
            Q0=makeQuery(id+"F1.opExtrude","SWEPT_BODY",BODY,{"disambiguationData":[OSD([sQuery(id+"F0.wireOp",EDGE,"E0.1"),sQuery(id+"F0.wireOp",EDGE,"E3.0.5.0"),sQuery(id+"F0.wireOp",EDGE,"E5"),sQuery(id+"F0.wireOp",EDGE,"E18")])]});
            var Q1;
            Q1=makeQuery(id+"F2.opExtrude","SWEPT_BODY",BODY,{"disambiguationData":[OSD([sQuery(id+"F0.wireOp",EDGE,"E0.1"),sQuery(id+"F0.wireOp",EDGE,"E4"),sQuery(id+"F0.wireOp",EDGE,"E6"),sQuery(id+"F0.wireOp",EDGE,"E8")])]});
            var Q2;
            Q2=makeQuery(id+"F1.opExtrude","SWEPT_BODY",BODY,{"disambiguationData":[OSD([sQuery(id+"F0.wireOp",EDGE,"E4"),sQuery(id+"F0.wireOp",EDGE,"E6"),sQuery(id+"F0.wireOp",EDGE,"E7"),sQuery(id+"F0.wireOp",EDGE,"E8")])]});
            var Q3;
            Q3=makeQuery(id+"F1.opExtrude","SWEPT_BODY",BODY,{"disambiguationData":[OSD([sQuery(id+"F0.wireOp",EDGE,"E3.0.1.0"),sQuery(id+"F0.wireOp",EDGE,"E3.0.2.0"),sQuery(id+"F0.wireOp",EDGE,"E5"),sQuery(id+"F0.wireOp",EDGE,"E18")])]});
            var Q4;
            Q4=makeQuery(id+"F1.opExtrude","SWEPT_BODY",BODY,{"disambiguationData":[OSD([sQuery(id+"F0.wireOp",EDGE,"E3.0.3.0"),sQuery(id+"F0.wireOp",EDGE,"E3.0.4.0"),sQuery(id+"F0.wireOp",EDGE,"E5"),sQuery(id+"F0.wireOp",EDGE,"E18")])]});
            var Q5;
            Q5=makeQuery(id+"F2.opExtrude","SWEPT_BODY",BODY,{"disambiguationData":[OSD([sQuery(id+"F0.wireOp",EDGE,"E2"),sQuery(id+"F0.wireOp",EDGE,"E4"),sQuery(id+"F0.wireOp",EDGE,"E7"),sQuery(id+"F0.wireOp",EDGE,"E8")])]});
            var Q6;
            Q6=makeQuery(id+"F2.opExtrude","SWEPT_BODY",BODY,{"disambiguationData":[OSD([sQuery(id+"F0.wireOp",EDGE,"E3.0.4.0"),sQuery(id+"F0.wireOp",EDGE,"E3.0.5.0"),sQuery(id+"F0.wireOp",EDGE,"E5"),sQuery(id+"F0.wireOp",EDGE,"E18")])]});
            var Q7;
            Q7=makeQuery(id+"F2.opExtrude","SWEPT_BODY",BODY,{"disambiguationData":[OSD([sQuery(id+"F0.wireOp",EDGE,"E3.0.2.0"),sQuery(id+"F0.wireOp",EDGE,"E3.0.3.0"),sQuery(id+"F0.wireOp",EDGE,"E5"),sQuery(id+"F0.wireOp",EDGE,"E18")])]});
            var Q8;
            Q8=makeQuery(id+"F3.opExtrude","SWEPT_BODY",BODY,{"disambiguationData":[OSD([sQuery(id+"F0.wireOp",EDGE,"E0.1"),sQuery(id+"F0.wireOp",EDGE,"E6"),sQuery(id+"F0.wireOp",EDGE,"E15"),sQuery(id+"F0.wireOp",EDGE,"E16")])]});
            var Q9;
            Q9=makeQuery(id+"F1.opExtrude","SWEPT_BODY",BODY,{"disambiguationData":[OSD([sQuery(id+"F0.wireOp",EDGE,"E0.1"),sQuery(id+"F0.wireOp",EDGE,"E3.0.5.0"),sQuery(id+"F0.wireOp",EDGE,"E13.2.0.0"),sQuery(id+"F0.wireOp",EDGE,"E13.3.0.0")])]});
            var Q10;
            Q10=makeQuery(id+"F1.opExtrude","SWEPT_BODY",BODY,{"disambiguationData":[OSD([sQuery(id+"F0.wireOp",EDGE,"E0.1"),sQuery(id+"F0.wireOp",EDGE,"E6"),sQuery(id+"F0.wireOp",EDGE,"E8"),sQuery(id+"F0.wireOp",EDGE,"E16")])]});
            var Q11;
            Q11=makeQuery(id+"F1.opExtrude","SWEPT_BODY",BODY,{"disambiguationData":[OSD([sQuery(id+"F0.wireOp",EDGE,"E0.1"),sQuery(id+"F0.wireOp",EDGE,"E6"),sQuery(id+"F0.wireOp",EDGE,"E14"),sQuery(id+"F0.wireOp",EDGE,"E15")])]});
            var Q12;
            Q12=makeQuery(id+"F1.opExtrude","SWEPT_BODY",BODY,{"disambiguationData":[OSD([sQuery(id+"F0.wireOp",EDGE,"E0.1"),sQuery(id+"F0.wireOp",EDGE,"E3.0.5.0"),sQuery(id+"F0.wireOp",EDGE,"E12"),sQuery(id+"F0.wireOp",EDGE,"E13.1.0.0")])]});
            var Q13;
            Q13=makeQuery(id+"F1.opExtrude","SWEPT_BODY",BODY,{"disambiguationData":[OSD([sQuery(id+"F0.wireOp",EDGE,"E2"),sQuery(id+"F0.wireOp",EDGE,"E4"),sQuery(id+"F0.wireOp",EDGE,"E7"),sQuery(id+"F0.wireOp",EDGE,"E8")])]});
            var Q14;
            Q14=makeQuery(id+"F1.opExtrude","SWEPT_BODY",BODY,{"disambiguationData":[OSD([sQuery(id+"F0.wireOp",EDGE,"E3.0.1.0"),sQuery(id+"F0.wireOp",EDGE,"E3.0.2.0"),sQuery(id+"F0.wireOp",EDGE,"E13.2.0.0"),sQuery(id+"F0.wireOp",EDGE,"E13.3.0.0")])]});
            var Q15;
            Q15=makeQuery(id+"F1.opExtrude","SWEPT_BODY",BODY,{"disambiguationData":[OSD([sQuery(id+"F0.wireOp",EDGE,"E3.0.1.0"),sQuery(id+"F0.wireOp",EDGE,"E3.0.2.0"),sQuery(id+"F0.wireOp",EDGE,"E12"),sQuery(id+"F0.wireOp",EDGE,"E13.1.0.0")])]});
            var Q16;
            Q16=makeQuery(id+"F1.opExtrude","SWEPT_BODY",BODY,{"disambiguationData":[OSD([sQuery(id+"F0.wireOp",EDGE,"E3.0.2.0"),sQuery(id+"F0.wireOp",EDGE,"E3.0.3.0"),sQuery(id+"F0.wireOp",EDGE,"E5"),sQuery(id+"F0.wireOp",EDGE,"E13.3.0.0")])]});
            var Q17;
            Q17=makeQuery(id+"F1.opExtrude","SWEPT_BODY",BODY,{"disambiguationData":[OSD([sQuery(id+"F0.wireOp",EDGE,"E3.0.2.0"),sQuery(id+"F0.wireOp",EDGE,"E3.0.3.0"),sQuery(id+"F0.wireOp",EDGE,"E13.1.0.0"),sQuery(id+"F0.wireOp",EDGE,"E13.2.0.0")])]});
            var Q18;
            Q18=makeQuery(id+"F1.opExtrude","SWEPT_BODY",BODY,{"disambiguationData":[OSD([sQuery(id+"F0.wireOp",EDGE,"E3.0.3.0"),sQuery(id+"F0.wireOp",EDGE,"E3.0.4.0"),sQuery(id+"F0.wireOp",EDGE,"E13.2.0.0"),sQuery(id+"F0.wireOp",EDGE,"E13.3.0.0")])]});
            var Q19;
            Q19=makeQuery(id+"F1.opExtrude","SWEPT_BODY",BODY,{"disambiguationData":[OSD([sQuery(id+"F0.wireOp",EDGE,"E3.0.3.0"),sQuery(id+"F0.wireOp",EDGE,"E3.0.4.0"),sQuery(id+"F0.wireOp",EDGE,"E12"),sQuery(id+"F0.wireOp",EDGE,"E13.1.0.0")])]});
            var Q20;
            Q20=makeQuery(id+"F1.opExtrude","SWEPT_BODY",BODY,{"disambiguationData":[OSD([sQuery(id+"F0.wireOp",EDGE,"E3.0.4.0"),sQuery(id+"F0.wireOp",EDGE,"E3.0.5.0"),sQuery(id+"F0.wireOp",EDGE,"E5"),sQuery(id+"F0.wireOp",EDGE,"E13.3.0.0")])]});
            var Q21;
            Q21=makeQuery(id+"F2.opExtrude","SWEPT_BODY",BODY,{"disambiguationData":[OSD([sQuery(id+"F0.wireOp",EDGE,"E0.1"),sQuery(id+"F0.wireOp",EDGE,"E3.0.5.0"),sQuery(id+"F0.wireOp",EDGE,"E13.1.0.0"),sQuery(id+"F0.wireOp",EDGE,"E13.2.0.0")])]});
            var Q22;
            Q22=makeQuery(id+"F2.opExtrude","SWEPT_BODY",BODY,{"disambiguationData":[OSD([sQuery(id+"F0.wireOp",EDGE,"E0.1"),sQuery(id+"F0.wireOp",EDGE,"E3.0.5.0"),sQuery(id+"F0.wireOp",EDGE,"E5"),sQuery(id+"F0.wireOp",EDGE,"E13.3.0.0")])]});
            var Q23;
            Q23=makeQuery(id+"F2.opExtrude","SWEPT_BODY",BODY,{"disambiguationData":[OSD([sQuery(id+"F0.wireOp",EDGE,"E0.1"),sQuery(id+"F0.wireOp",EDGE,"E4"),sQuery(id+"F0.wireOp",EDGE,"E6"),sQuery(id+"F0.wireOp",EDGE,"E14")])]});
            var Q24;
            Q24=makeQuery(id+"F3.opExtrude","SWEPT_BODY",BODY,{"disambiguationData":[OSD([sQuery(id+"F0.wireOp",EDGE,"E3.0.2.0"),sQuery(id+"F0.wireOp",EDGE,"E3.0.3.0"),sQuery(id+"F0.wireOp",EDGE,"E12"),sQuery(id+"F0.wireOp",EDGE,"E13.1.0.0")])]});
            var Q25;
            Q25=makeQuery(id+"F3.opExtrude","SWEPT_BODY",BODY,{"disambiguationData":[OSD([sQuery(id+"F0.wireOp",EDGE,"E3.0.4.0"),sQuery(id+"F0.wireOp",EDGE,"E3.0.5.0"),sQuery(id+"F0.wireOp",EDGE,"E12"),sQuery(id+"F0.wireOp",EDGE,"E13.1.0.0")])]});
            var Q26;
            Q26=makeQuery(id+"F3.opExtrude","SWEPT_BODY",BODY,{"disambiguationData":[OSD([sQuery(id+"F0.wireOp",EDGE,"E4"),sQuery(id+"F0.wireOp",EDGE,"E6"),sQuery(id+"F0.wireOp",EDGE,"E7"),sQuery(id+"F0.wireOp",EDGE,"E15")])]});
            var Q27;
            Q27=makeQuery(id+"F3.opExtrude","SWEPT_BODY",BODY,{"disambiguationData":[OSD([sQuery(id+"F0.wireOp",EDGE,"E6"),sQuery(id+"F0.wireOp",EDGE,"E7"),sQuery(id+"F0.wireOp",EDGE,"E8"),sQuery(id+"F0.wireOp",EDGE,"E16")])]});
            var Q28;
            Q28=makeQuery(id+"F2.opExtrude","SWEPT_BODY",BODY,{"disambiguationData":[OSD([sQuery(id+"F0.wireOp",EDGE,"E3.0.1.0"),sQuery(id+"F0.wireOp",EDGE,"E3.0.2.0"),sQuery(id+"F0.wireOp",EDGE,"E13.1.0.0"),sQuery(id+"F0.wireOp",EDGE,"E13.2.0.0")])]});
            var Q29;
            Q29=makeQuery(id+"F2.opExtrude","SWEPT_BODY",BODY,{"disambiguationData":[OSD([sQuery(id+"F0.wireOp",EDGE,"E6"),sQuery(id+"F0.wireOp",EDGE,"E7"),sQuery(id+"F0.wireOp",EDGE,"E15"),sQuery(id+"F0.wireOp",EDGE,"E16")])]});
            var Q30;
            Q30=makeQuery(id+"F2.opExtrude","SWEPT_BODY",BODY,{"disambiguationData":[OSD([sQuery(id+"F0.wireOp",EDGE,"E3.0.1.0"),sQuery(id+"F0.wireOp",EDGE,"E3.0.2.0"),sQuery(id+"F0.wireOp",EDGE,"E5"),sQuery(id+"F0.wireOp",EDGE,"E13.3.0.0")])]});
            var Q31;
            Q31=makeQuery(id+"F2.opExtrude","SWEPT_BODY",BODY,{"disambiguationData":[OSD([sQuery(id+"F0.wireOp",EDGE,"E3.0.4.0"),sQuery(id+"F0.wireOp",EDGE,"E3.0.5.0"),sQuery(id+"F0.wireOp",EDGE,"E13.2.0.0"),sQuery(id+"F0.wireOp",EDGE,"E13.3.0.0")])]});
            var Q32;
            Q32=makeQuery(id+"F2.opExtrude","SWEPT_BODY",BODY,{"disambiguationData":[OSD([sQuery(id+"F0.wireOp",EDGE,"E3.0.3.0"),sQuery(id+"F0.wireOp",EDGE,"E3.0.4.0"),sQuery(id+"F0.wireOp",EDGE,"E13.1.0.0"),sQuery(id+"F0.wireOp",EDGE,"E13.2.0.0")])]});
            var Q33;
            Q33=makeQuery(id+"F2.opExtrude","SWEPT_BODY",BODY,{"disambiguationData":[OSD([sQuery(id+"F0.wireOp",EDGE,"E3.0.3.0"),sQuery(id+"F0.wireOp",EDGE,"E3.0.4.0"),sQuery(id+"F0.wireOp",EDGE,"E5"),sQuery(id+"F0.wireOp",EDGE,"E13.3.0.0")])]});
            var Q34;
            Q34=makeQuery(id+"F2.opExtrude","SWEPT_BODY",BODY,{"disambiguationData":[OSD([sQuery(id+"F0.wireOp",EDGE,"E3.0.2.0"),sQuery(id+"F0.wireOp",EDGE,"E3.0.3.0"),sQuery(id+"F0.wireOp",EDGE,"E13.2.0.0"),sQuery(id+"F0.wireOp",EDGE,"E13.3.0.0")])]});
            var Q35;
            Q35=makeQuery(id+"F1.opExtrude","SWEPT_BODY",BODY,{"disambiguationData":[OSD([sQuery(id+"F0.wireOp",EDGE,"E3.0.4.0"),sQuery(id+"F0.wireOp",EDGE,"E3.0.5.0"),sQuery(id+"F0.wireOp",EDGE,"E13.1.0.0"),sQuery(id+"F0.wireOp",EDGE,"E13.2.0.0")])]});
            transform(context, id + "F15", {"entities" : qUnion([Q0, Q1, Q2, Q3, Q4, Q5, Q6, Q7, Q8, Q9, Q10, Q11, Q12, Q13, Q14, Q15, Q16, Q17, Q18, Q19, Q20, Q21, Q22, Q23, Q24, Q25, Q26, Q27, Q28, Q29, Q30, Q31, Q32, Q33, Q34, Q35]), "transformType" : TransformType.TRANSLATION_3D, "dx" : 0 * mm, "dy" : -getVariable(context, 'd'), "dz" : 0 * mm, "makeCopy" : false});
        }
        {
            var Q0;
            Q0=makeQuery(id+"F1.opExtrude","SWEPT_BODY",BODY,{"disambiguationData":[OSD([sQuery(id+"F0.wireOp",EDGE,"E4"),sQuery(id+"F0.wireOp",EDGE,"E6"),sQuery(id+"F0.wireOp",EDGE,"E7"),sQuery(id+"F0.wireOp",EDGE,"E8")])]});
            var Q1;
            Q1=makeQuery(id+"F2.opExtrude","SWEPT_BODY",BODY,{"disambiguationData":[OSD([sQuery(id+"F0.wireOp",EDGE,"E2"),sQuery(id+"F0.wireOp",EDGE,"E4"),sQuery(id+"F0.wireOp",EDGE,"E7"),sQuery(id+"F0.wireOp",EDGE,"E8")])]});
            var Q2;
            Q2=makeQuery(id+"F1.opExtrude","SWEPT_BODY",BODY,{"disambiguationData":[OSD([sQuery(id+"F0.wireOp",EDGE,"E2"),sQuery(id+"F0.wireOp",EDGE,"E4"),sQuery(id+"F0.wireOp",EDGE,"E7"),sQuery(id+"F0.wireOp",EDGE,"E8")])]});
            var Q3;
            Q3=makeQuery(id+"F3.opExtrude","SWEPT_BODY",BODY,{"disambiguationData":[OSD([sQuery(id+"F0.wireOp",EDGE,"E4"),sQuery(id+"F0.wireOp",EDGE,"E6"),sQuery(id+"F0.wireOp",EDGE,"E7"),sQuery(id+"F0.wireOp",EDGE,"E15")])]});
            var Q4;
            Q4=makeQuery(id+"F3.opExtrude","SWEPT_BODY",BODY,{"disambiguationData":[OSD([sQuery(id+"F0.wireOp",EDGE,"E6"),sQuery(id+"F0.wireOp",EDGE,"E7"),sQuery(id+"F0.wireOp",EDGE,"E8"),sQuery(id+"F0.wireOp",EDGE,"E16")])]});
            var Q5;
            Q5=makeQuery(id+"F2.opExtrude","SWEPT_BODY",BODY,{"disambiguationData":[OSD([sQuery(id+"F0.wireOp",EDGE,"E6"),sQuery(id+"F0.wireOp",EDGE,"E7"),sQuery(id+"F0.wireOp",EDGE,"E15"),sQuery(id+"F0.wireOp",EDGE,"E16")])]});
            transform(context, id + "F16", {"entities" : qUnion([Q0, Q1, Q2, Q3, Q4, Q5]), "transformType" : TransformType.TRANSLATION_3D, "dx" : 0 * mm, "dy" : -getVariable(context, 'd'), "dz" : 0 * mm, "makeCopy" : false});
        }
        {
            var Q0;
            Q0=makeQuery(id+"F2.opExtrude","SWEPT_BODY",BODY,{"disambiguationData":[OSD([sQuery(id+"F0.wireOp",EDGE,"E4"),sQuery(id+"F0.wireOp",EDGE,"E9"),sQuery(id+"F0.wireOp",EDGE,"E12")])]});
            var Q1;
            Q1=makeQuery(id+"F3.opExtrude","SWEPT_BODY",BODY,{"disambiguationData":[OSD([sQuery(id+"F0.wireOp",EDGE,"E1"),sQuery(id+"F0.wireOp",EDGE,"E3.0.1.0"),sQuery(id+"F0.wireOp",EDGE,"E12"),sQuery(id+"F0.wireOp",EDGE,"E13.1.0.0")])]});
            var Q2;
            Q2=makeQuery(id+"F2.opExtrude","SWEPT_BODY",BODY,{"disambiguationData":[OSD([sQuery(id+"F0.wireOp",EDGE,"E0.1"),sQuery(id+"F0.wireOp",EDGE,"E4"),sQuery(id+"F0.wireOp",EDGE,"E6"),sQuery(id+"F0.wireOp",EDGE,"E14")])]});
            var Q3;
            Q3=makeQuery(id+"F1.opExtrude","SWEPT_BODY",BODY,{"disambiguationData":[OSD([sQuery(id+"F0.wireOp",EDGE,"E0.1"),sQuery(id+"F0.wireOp",EDGE,"E6"),sQuery(id+"F0.wireOp",EDGE,"E14"),sQuery(id+"F0.wireOp",EDGE,"E15")])]});
            var Q4;
            Q4=makeQuery(id+"F3.opExtrude","SWEPT_BODY",BODY,{"disambiguationData":[OSD([sQuery(id+"F0.wireOp",EDGE,"E0.1"),sQuery(id+"F0.wireOp",EDGE,"E6"),sQuery(id+"F0.wireOp",EDGE,"E15"),sQuery(id+"F0.wireOp",EDGE,"E16")])]});
            var Q5;
            Q5=makeQuery(id+"F1.opExtrude","SWEPT_BODY",BODY,{"disambiguationData":[OSD([sQuery(id+"F0.wireOp",EDGE,"E1"),sQuery(id+"F0.wireOp",EDGE,"E3.0.1.0"),sQuery(id+"F0.wireOp",EDGE,"E13.1.0.0"),sQuery(id+"F0.wireOp",EDGE,"E13.2.0.0")])]});
            var Q6;
            Q6=makeQuery(id+"F3.opExtrude","SWEPT_BODY",BODY,{"disambiguationData":[OSD([sQuery(id+"F0.wireOp",EDGE,"E1"),sQuery(id+"F0.wireOp",EDGE,"E3.0.1.0"),sQuery(id+"F0.wireOp",EDGE,"E13.2.0.0"),sQuery(id+"F0.wireOp",EDGE,"E13.3.0.0")])]});
            var Q7;
            Q7=makeQuery(id+"F1.opExtrude","SWEPT_BODY",BODY,{"disambiguationData":[OSD([sQuery(id+"F0.wireOp",EDGE,"E3.0.1.0"),sQuery(id+"F0.wireOp",EDGE,"E3.0.2.0"),sQuery(id+"F0.wireOp",EDGE,"E13.2.0.0"),sQuery(id+"F0.wireOp",EDGE,"E13.3.0.0")])]});
            var Q8;
            Q8=makeQuery(id+"F3.opExtrude","SWEPT_BODY",BODY,{"disambiguationData":[OSD([sQuery(id+"F0.wireOp",EDGE,"E3.0.2.0"),sQuery(id+"F0.wireOp",EDGE,"E3.0.3.0"),sQuery(id+"F0.wireOp",EDGE,"E12"),sQuery(id+"F0.wireOp",EDGE,"E13.1.0.0")])]});
            var Q9;
            Q9=makeQuery(id+"F3.opExtrude","SWEPT_BODY",BODY,{"disambiguationData":[OSD([sQuery(id+"F0.wireOp",EDGE,"E3.0.4.0"),sQuery(id+"F0.wireOp",EDGE,"E3.0.5.0"),sQuery(id+"F0.wireOp",EDGE,"E12"),sQuery(id+"F0.wireOp",EDGE,"E13.1.0.0")])]});
            var Q10;
            Q10=makeQuery(id+"F1.opExtrude","SWEPT_BODY",BODY,{"disambiguationData":[OSD([sQuery(id+"F0.wireOp",EDGE,"E3.0.1.0"),sQuery(id+"F0.wireOp",EDGE,"E3.0.2.0"),sQuery(id+"F0.wireOp",EDGE,"E12"),sQuery(id+"F0.wireOp",EDGE,"E13.1.0.0")])]});
            var Q11;
            Q11=makeQuery(id+"F1.opExtrude","SWEPT_BODY",BODY,{"disambiguationData":[OSD([sQuery(id+"F0.wireOp",EDGE,"E3.0.2.0"),sQuery(id+"F0.wireOp",EDGE,"E3.0.3.0"),sQuery(id+"F0.wireOp",EDGE,"E5"),sQuery(id+"F0.wireOp",EDGE,"E13.3.0.0")])]});
            var Q12;
            Q12=makeQuery(id+"F1.opExtrude","SWEPT_BODY",BODY,{"disambiguationData":[OSD([sQuery(id+"F0.wireOp",EDGE,"E3.0.2.0"),sQuery(id+"F0.wireOp",EDGE,"E3.0.3.0"),sQuery(id+"F0.wireOp",EDGE,"E13.1.0.0"),sQuery(id+"F0.wireOp",EDGE,"E13.2.0.0")])]});
            var Q13;
            Q13=makeQuery(id+"F1.opExtrude","SWEPT_BODY",BODY,{"disambiguationData":[OSD([sQuery(id+"F0.wireOp",EDGE,"E0.1"),sQuery(id+"F0.wireOp",EDGE,"E3.0.5.0"),sQuery(id+"F0.wireOp",EDGE,"E13.2.0.0"),sQuery(id+"F0.wireOp",EDGE,"E13.3.0.0")])]});
            var Q14;
            Q14=makeQuery(id+"F1.opExtrude","SWEPT_BODY",BODY,{"disambiguationData":[OSD([sQuery(id+"F0.wireOp",EDGE,"E3.0.3.0"),sQuery(id+"F0.wireOp",EDGE,"E3.0.4.0"),sQuery(id+"F0.wireOp",EDGE,"E13.2.0.0"),sQuery(id+"F0.wireOp",EDGE,"E13.3.0.0")])]});
            var Q15;
            Q15=makeQuery(id+"F1.opExtrude","SWEPT_BODY",BODY,{"disambiguationData":[OSD([sQuery(id+"F0.wireOp",EDGE,"E3.0.3.0"),sQuery(id+"F0.wireOp",EDGE,"E3.0.4.0"),sQuery(id+"F0.wireOp",EDGE,"E12"),sQuery(id+"F0.wireOp",EDGE,"E13.1.0.0")])]});
            var Q16;
            Q16=makeQuery(id+"F1.opExtrude","SWEPT_BODY",BODY,{"disambiguationData":[OSD([sQuery(id+"F0.wireOp",EDGE,"E3.0.4.0"),sQuery(id+"F0.wireOp",EDGE,"E3.0.5.0"),sQuery(id+"F0.wireOp",EDGE,"E5"),sQuery(id+"F0.wireOp",EDGE,"E13.3.0.0")])]});
            var Q17;
            Q17=makeQuery(id+"F1.opExtrude","SWEPT_BODY",BODY,{"disambiguationData":[OSD([sQuery(id+"F0.wireOp",EDGE,"E3.0.4.0"),sQuery(id+"F0.wireOp",EDGE,"E3.0.5.0"),sQuery(id+"F0.wireOp",EDGE,"E13.1.0.0"),sQuery(id+"F0.wireOp",EDGE,"E13.2.0.0")])]});
            var Q18;
            Q18=makeQuery(id+"F2.opExtrude","SWEPT_BODY",BODY,{"disambiguationData":[OSD([sQuery(id+"F0.wireOp",EDGE,"E0.1"),sQuery(id+"F0.wireOp",EDGE,"E3.0.5.0"),sQuery(id+"F0.wireOp",EDGE,"E5"),sQuery(id+"F0.wireOp",EDGE,"E13.3.0.0")])]});
            var Q19;
            Q19=makeQuery(id+"F2.opExtrude","SWEPT_BODY",BODY,{"disambiguationData":[OSD([sQuery(id+"F0.wireOp",EDGE,"E0.1"),sQuery(id+"F0.wireOp",EDGE,"E3.0.5.0"),sQuery(id+"F0.wireOp",EDGE,"E13.1.0.0"),sQuery(id+"F0.wireOp",EDGE,"E13.2.0.0")])]});
            var Q20;
            Q20=makeQuery(id+"F2.opExtrude","SWEPT_BODY",BODY,{"disambiguationData":[OSD([sQuery(id+"F0.wireOp",EDGE,"E3.0.1.0"),sQuery(id+"F0.wireOp",EDGE,"E3.0.2.0"),sQuery(id+"F0.wireOp",EDGE,"E5"),sQuery(id+"F0.wireOp",EDGE,"E13.3.0.0")])]});
            var Q21;
            Q21=makeQuery(id+"F2.opExtrude","SWEPT_BODY",BODY,{"disambiguationData":[OSD([sQuery(id+"F0.wireOp",EDGE,"E3.0.1.0"),sQuery(id+"F0.wireOp",EDGE,"E3.0.2.0"),sQuery(id+"F0.wireOp",EDGE,"E13.1.0.0"),sQuery(id+"F0.wireOp",EDGE,"E13.2.0.0")])]});
            var Q22;
            Q22=makeQuery(id+"F2.opExtrude","SWEPT_BODY",BODY,{"disambiguationData":[OSD([sQuery(id+"F0.wireOp",EDGE,"E3.0.2.0"),sQuery(id+"F0.wireOp",EDGE,"E3.0.3.0"),sQuery(id+"F0.wireOp",EDGE,"E13.2.0.0"),sQuery(id+"F0.wireOp",EDGE,"E13.3.0.0")])]});
            var Q23;
            Q23=makeQuery(id+"F2.opExtrude","SWEPT_BODY",BODY,{"disambiguationData":[OSD([sQuery(id+"F0.wireOp",EDGE,"E3.0.3.0"),sQuery(id+"F0.wireOp",EDGE,"E3.0.4.0"),sQuery(id+"F0.wireOp",EDGE,"E13.1.0.0"),sQuery(id+"F0.wireOp",EDGE,"E13.2.0.0")])]});
            var Q24;
            Q24=makeQuery(id+"F2.opExtrude","SWEPT_BODY",BODY,{"disambiguationData":[OSD([sQuery(id+"F0.wireOp",EDGE,"E3.0.3.0"),sQuery(id+"F0.wireOp",EDGE,"E3.0.4.0"),sQuery(id+"F0.wireOp",EDGE,"E5"),sQuery(id+"F0.wireOp",EDGE,"E13.3.0.0")])]});
            var Q25;
            Q25=makeQuery(id+"F1.opExtrude","SWEPT_BODY",BODY,{"disambiguationData":[OSD([sQuery(id+"F0.wireOp",EDGE,"E0.1"),sQuery(id+"F0.wireOp",EDGE,"E3.0.5.0"),sQuery(id+"F0.wireOp",EDGE,"E12"),sQuery(id+"F0.wireOp",EDGE,"E13.1.0.0")])]});
            var Q26;
            Q26=makeQuery(id+"F2.opExtrude","SWEPT_BODY",BODY,{"disambiguationData":[OSD([sQuery(id+"F0.wireOp",EDGE,"E3.0.4.0"),sQuery(id+"F0.wireOp",EDGE,"E3.0.5.0"),sQuery(id+"F0.wireOp",EDGE,"E13.2.0.0"),sQuery(id+"F0.wireOp",EDGE,"E13.3.0.0")])]});
            transform(context, id + "F17", {"entities" : qUnion([Q0, Q1, Q2, Q3, Q4, Q5, Q6, Q7, Q8, Q9, Q10, Q11, Q12, Q13, Q14, Q15, Q16, Q17, Q18, Q19, Q20, Q21, Q22, Q23, Q24, Q25, Q26]), "transformType" : TransformType.TRANSLATION_3D, "dx" : -getVariable(context, 'd'), "dy" : 0 * mm, "dz" : 0 * mm, "makeCopy" : false});
        }
    });
